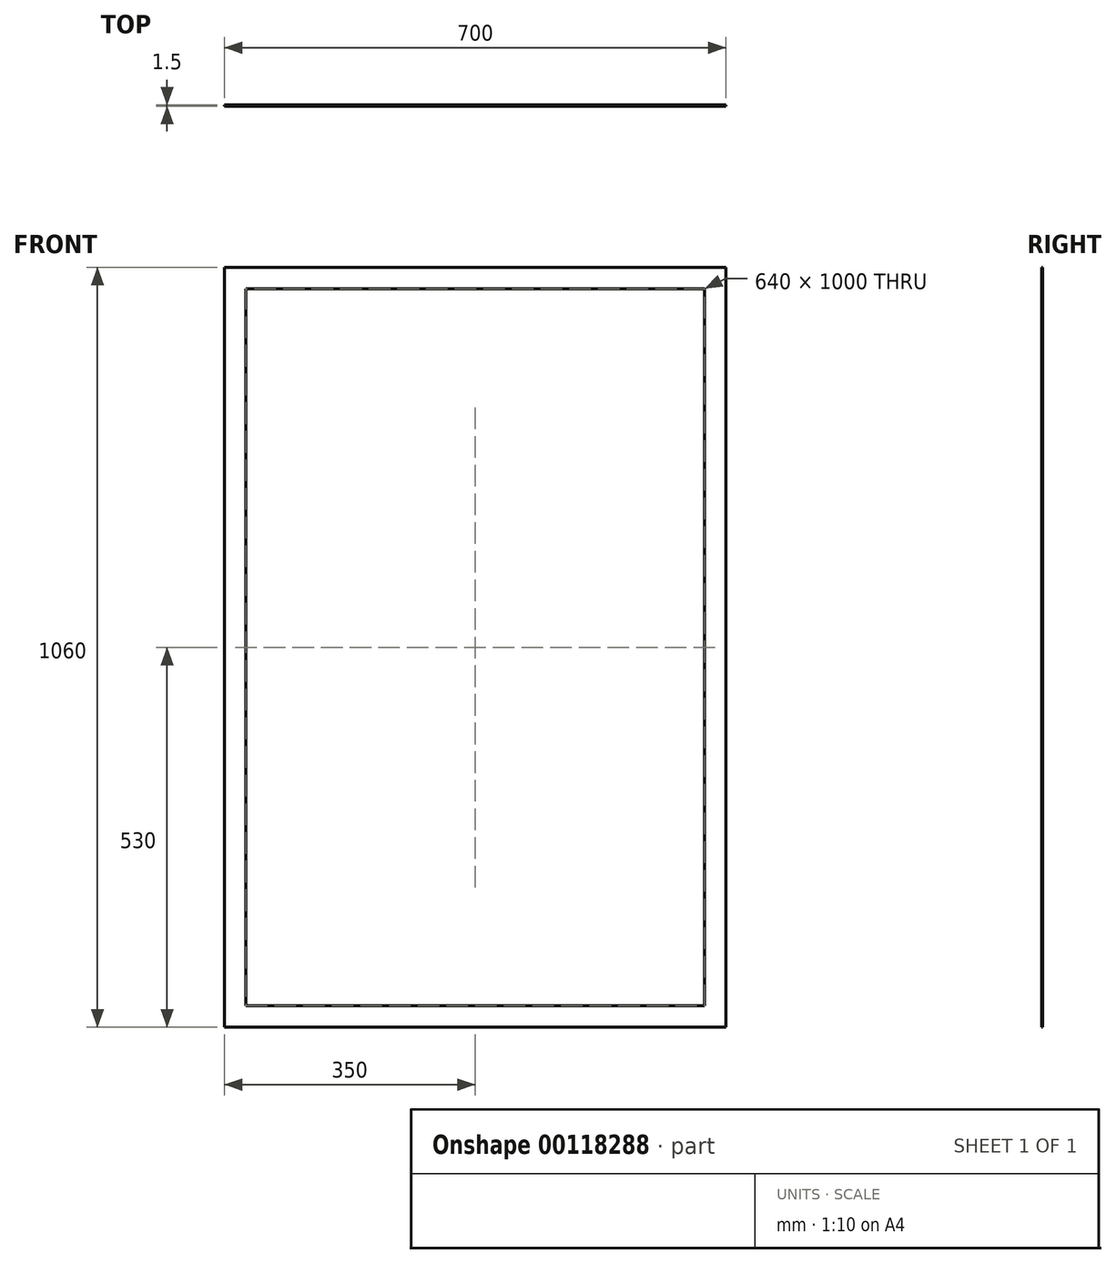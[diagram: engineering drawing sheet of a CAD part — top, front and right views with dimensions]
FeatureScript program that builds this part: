
annotation { "Feature Type Name" : "Feature", "Feature Type Description" : "" }
export const myFeature = defineFeature(function(context is Context, id is Id, definition is map)
    precondition{}
    {
        {
            var Q0;
            Q0=qCreatedBy(makeId("Front.planeOp"),FACE);
            var sketch = newSketch(context, id + "F0", { "sketchPlane" : qUnion([Q0])});
            skLineSegment(sketch, "E0.bottom", {"start": v(0, 0) * mm, "end": v(700, 0) * mm});
            skLineSegment(sketch, "E0.top", {"start": v(0, 1060) * mm, "end": v(700, 1060) * mm});
            skLineSegment(sketch, "E0.left", {"start": v(0, 0) * mm, "end": v(0, 1060) * mm});
            skLineSegment(sketch, "E0.right", {"start": v(700, 0) * mm, "end": v(700, 1060) * mm});
            skSolve(sketch);
        }
        {
            var Q0;
            Q0=makeQuery(id+"F0.imprint","IMPRINT",FACE,{"disambiguationData":[TD([[makeQuery(id+"F0.imprint","IMPRINT",EDGE,{"derivedFrom":sQuery(id+"F0.wireOp",EDGE,"E0.bottom")}),1.0]])]});
            extrude(context, id + "F1", {"entities" : qUnion([Q0]), "depth" : 1.5 * mm});
        }
        {
            var Q0;
            Q0=makeQuery(id+"F1.opExtrude","CAP_FACE",FACE,{"disambiguationData":[OSD([sQuery(id+"F0.wireOp",EDGE,"E0.bottom"),sQuery(id+"F0.wireOp",EDGE,"E0.top"),sQuery(id+"F0.wireOp",EDGE,"E0.left"),sQuery(id+"F0.wireOp",EDGE,"E0.right")])],"isStart":false});
            var sketch = newSketch(context, id + "F2", { "sketchPlane" : qUnion([Q0])});
            skLineSegment(sketch, "E1.0", {"start": v(30, 1030) * mm, "end": v(30, 30) * mm});
            skLineSegment(sketch, "E1.1", {"start": v(670, 1030) * mm, "end": v(30, 1030) * mm});
            skLineSegment(sketch, "E1.2", {"start": v(670, 30) * mm, "end": v(670, 1030) * mm});
            skLineSegment(sketch, "E1.3", {"start": v(30, 30) * mm, "end": v(670, 30) * mm});
            skLineSegment(sketch, "E2.bottom", {"start": v(30, 1030) * mm, "end": v(670, 1030) * mm});
            skLineSegment(sketch, "E2.top", {"start": v(30, 930) * mm, "end": v(670, 930) * mm});
            skLineSegment(sketch, "E2.left", {"start": v(30, 1030) * mm, "end": v(30, 930) * mm});
            skLineSegment(sketch, "E2.right", {"start": v(670, 1030) * mm, "end": v(670, 930) * mm});
            skSolve(sketch);
        }
        {
            var Q0;
            Q0=makeQuery(id+"F2.imprint","IMPRINT",FACE,{"disambiguationData":[TD([[makeQuery(id+"F2.imprint","IMPRINT",EDGE,{"derivedFrom":sQuery(id+"F2.wireOp",EDGE,"E1.0")}),1.0]])]});
            extrude(context, id + "F3", {"entities" : qUnion([Q0]), "operationType" : NewBodyOperationType.REMOVE, "oppositeDirection" : true, "depth" : 300.87 * mm});
        }
    });
